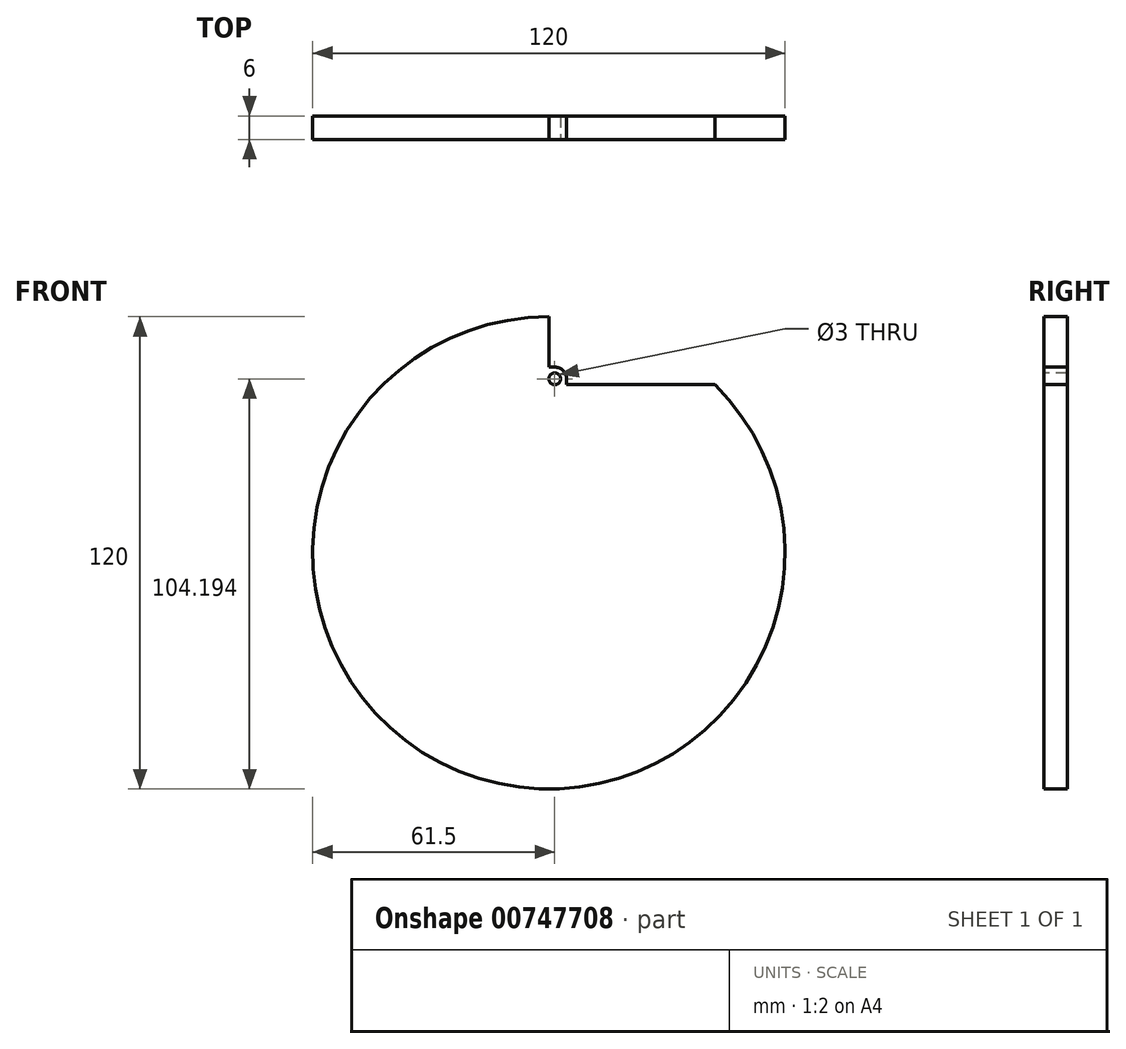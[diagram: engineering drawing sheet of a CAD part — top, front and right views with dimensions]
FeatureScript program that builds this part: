
annotation { "Feature Type Name" : "Feature", "Feature Type Description" : "" }
export const myFeature = defineFeature(function(context is Context, id is Id, definition is map)
    precondition{}
    {
        {
            var Q0;
            Q0=qCreatedBy(makeId("Front.planeOp"),FACE);
            var sketch = newSketch(context, id + "F0", { "sketchPlane" : qUnion([Q0])});
            skCircle(sketch, "E0", {"center": v(0, 0) * mm, "radius": 60 * mm});
            skSolve(sketch);
        }
        {
            var Q0;
            Q0=makeQuery(id+"F0.imprint","IMPRINT",FACE,{"disambiguationData":[TD([[makeQuery(id+"F0.imprint","IMPRINT",EDGE,{"derivedFrom":sQuery(id+"F0.wireOp",EDGE,"E0")}),1.0]])]});
            var sketch = newSketch(context, id + "F1", { "sketchPlane" : qUnion([Q0])});
            skLineSegment(sketch, "E1", {"start": v(0, 0) * mm, "end": v(0, 71.95) * mm, "construction": true});
            skLineSegment(sketch, "E2.1.0", {"start": v(0, 0) * mm, "end": v(-50.87, 50.87) * mm, "construction": true});
            skLineSegment(sketch, "E2.2.0", {"start": v(0, 0) * mm, "end": v(-71.95, 0) * mm, "construction": true});
            skLineSegment(sketch, "E2.3.0", {"start": v(0, 0) * mm, "end": v(-50.87, -50.87) * mm, "construction": true});
            skLineSegment(sketch, "E2.4.0", {"start": v(0, 0) * mm, "end": v(0, -71.95) * mm, "construction": true});
            skLineSegment(sketch, "E2.5.0", {"start": v(0, 0) * mm, "end": v(50.87, -50.87) * mm, "construction": true});
            skLineSegment(sketch, "E2.6.0", {"start": v(0, 0) * mm, "end": v(71.95, 0) * mm, "construction": true});
            skLineSegment(sketch, "E2.7.0", {"start": v(0, 0) * mm, "end": v(50.87, 50.87) * mm, "construction": true});
            skPoint(sketch, "E2.center", {"position": v(0, 0) * mm});
            skLineSegment(sketch, "E3", {"start": v(-42.7, 42.7) * mm, "end": v(42.7, 42.7) * mm, "construction": true});
            skSolve(sketch);
        }
        {
            var Q0;
            Q0=makeQuery(id+"F0.imprint","IMPRINT",FACE,{"disambiguationData":[TD([[makeQuery(id+"F0.imprint","IMPRINT",EDGE,{"derivedFrom":sQuery(id+"F0.wireOp",EDGE,"E0")}),1.0]])]});
            extrude(context, id + "F2", {"entities" : qUnion([Q0]), "depth" : 6 * mm, "offsetDistance" : 25 * mm});
        }
        {
            var Q0;
            Q0=makeQuery(id+"F2.opExtrude","CAP_FACE",FACE,{"disambiguationData":[OSD([sQuery(id+"F0.wireOp",EDGE,"E0")])],"isStart":false});
            var sketch = newSketch(context, id + "F3", { "sketchPlane" : qUnion([Q0])});
            skCircle(sketch, "E4", {"center": v(1.5, 44.2) * mm, "radius": 1.5 * mm});
            skSolve(sketch);
        }
        {
            var Q0;
            Q0=sQuery(id+"F3.wireOp",VERTEX,"E4.center");
            var Q1;
            Q1=makeQuery(id+"F2.opExtrude","SWEPT_BODY",BODY,{"disambiguationData":[OSD([sQuery(id+"F0.wireOp",EDGE,"E0")])]});
            hole(context, id + "F4", {"style" : HoleStyle.SIMPLE, "endStyle" : HoleEndStyle.THROUGH, "standardTappedOrClearance" : lookupTablePath({ "standard" : "ISO", "size" : "3", "type" : "Drilled" }), "standardBlindInLast" : lookupTablePath({ "standard" : "ISO", "size" : "3", "type" : "Drilled" }), "holeDiameter" : 3 * mm, "majorDiameter" : 5 * mm, "isTappedThrough" : true, "tappedDepth" : 12 * mm, "tapClearance" : 3, "locations" : qUnion([Q0]), "scope" : qUnion([Q1])});
        }
        {
            var Q0;
            Q0=makeQuery(id+"F2.opExtrude","CAP_FACE",FACE,{"disambiguationData":[OSD([sQuery(id+"F0.wireOp",EDGE,"E0")])],"isStart":false});
            var sketch = newSketch(context, id + "F5", { "sketchPlane" : qUnion([Q0])});
            skLineSegment(sketch, "E5", {"start": v(4.5, 42.7) * mm, "end": v(58.99, 42.7) * mm});
            skLineSegment(sketch, "E6", {"start": v(0, 64.22) * mm, "end": v(58.99, 64.22) * mm});
            skLineSegment(sketch, "E7", {"start": v(58.99, 64.22) * mm, "end": v(58.99, 42.7) * mm});
            skLineSegment(sketch, "E8", {"start": v(4.5, 44.2) * mm, "end": v(4.5, 42.7) * mm});
            skLineSegment(sketch, "E9", {"start": v(0, 64.22) * mm, "end": v(0, 47.2) * mm});
            skLineSegment(sketch, "E10", {"start": v(1.5, 47.2) * mm, "end": v(0, 47.2) * mm});
            skArc(sketch, "E11.trimOffspring", {"start": v(4.5, 44.2) * mm, "mid": v(3.62, 46.31) * mm, "end": v(1.5, 47.2) * mm});
            skPoint(sketch, "E12.orphan", {"position": v(0, 66.28) * mm});
            skSolve(sketch);
        }
        {
            var Q0;
            {var subQ6=sQuery(id+"F5.wireOp",EDGE,"E8");Q0=makeQuery(id+"F5.imprint","IMPRINT",FACE,{"disambiguationData":[TD([[makeQuery(id+"F5.imprint","IMPRINT",EDGE,{"derivedFrom":subQ6}),1.0]])]});}
            var Q1;
            {var subQ1=sQuery(id+"F5.wireOp",EDGE,"E6");Q1=makeQuery(id+"F5.imprint","IMPRINT",FACE,{"disambiguationData":[TD([[makeQuery(id+"F5.imprint","IMPRINT",EDGE,{"derivedFrom":subQ1}),-1.0]])]});}
            extrude(context, id + "F6", {"entities" : qUnion([Q0, Q1]), "operationType" : NewBodyOperationType.REMOVE, "oppositeDirection" : true, "depth" : 25 * mm, "offsetDistance" : 25 * mm});
        }
    });
